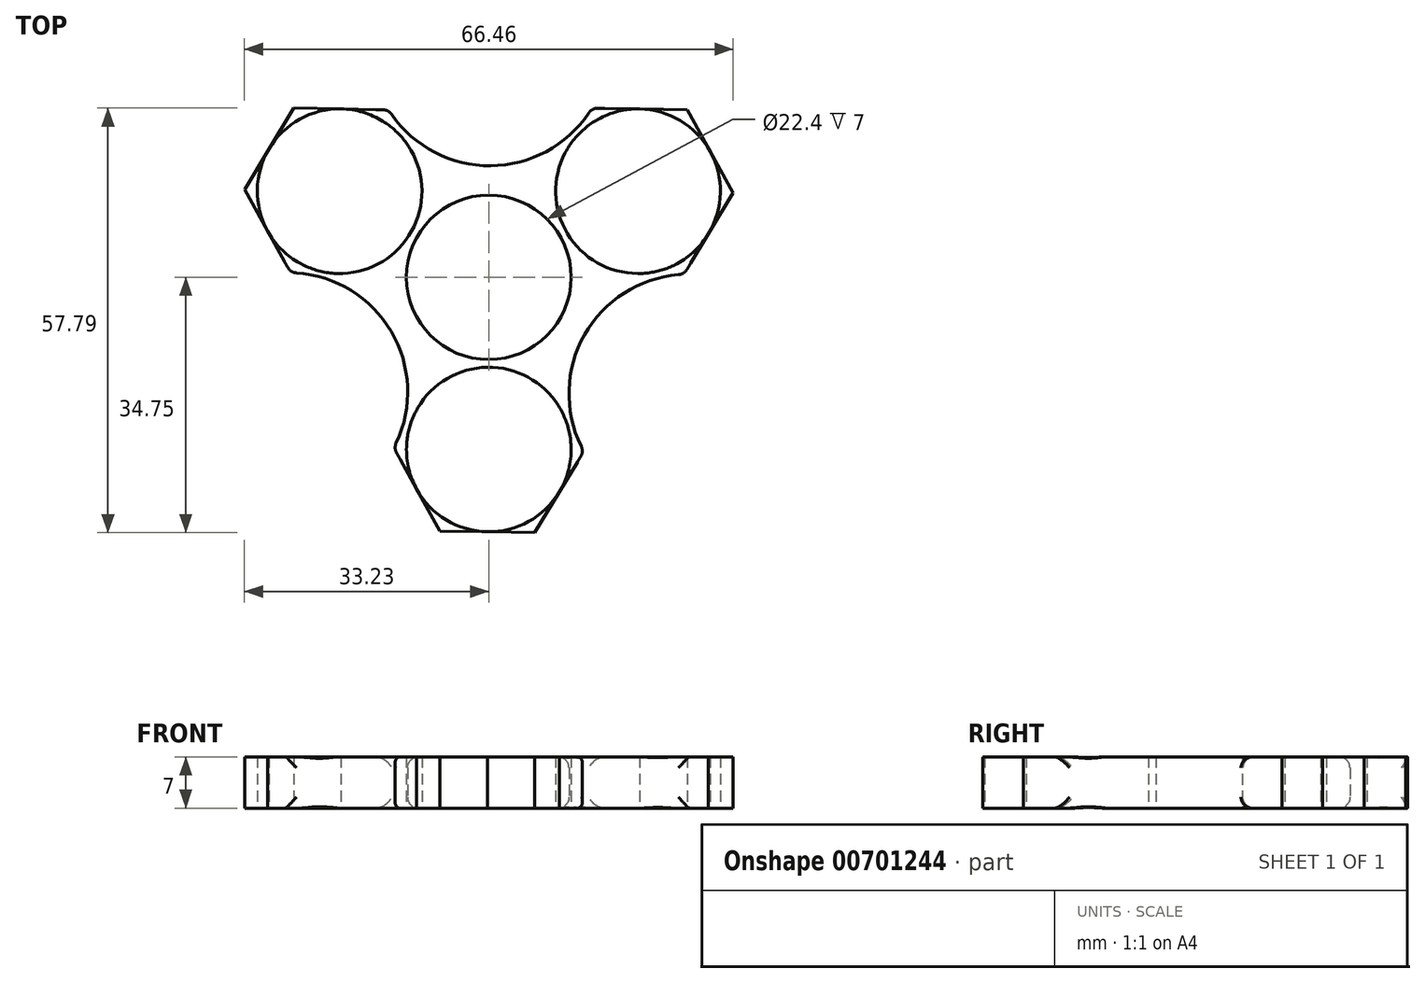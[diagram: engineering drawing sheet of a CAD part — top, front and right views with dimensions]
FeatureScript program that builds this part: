
annotation { "Feature Type Name" : "Feature", "Feature Type Description" : "" }
export const myFeature = defineFeature(function(context is Context, id is Id, definition is map)
    precondition{}
    {
        {
            var Q0;
            Q0=qCreatedBy(makeId("Top.planeOp"),FACE);
            var sketch = newSketch(context, id + "F0", { "sketchPlane" : qUnion([Q0])});
            skCircle(sketch, "E0", {"center": v(0, 0) * mm, "radius": 11.2 * mm});
            skCircle(sketch, "E1.cCircle", {"center": v(0, 0) * mm, "radius": 11.2 * mm, "construction": true});
            skLineSegment(sketch, "E1.0", {"start": v(12.93, -0.08) * mm, "end": v(6.4, -11.24) * mm});
            skLineSegment(sketch, "E1.1", {"start": v(6.4, -11.24) * mm, "end": v(-6.54, -11.16) * mm});
            skLineSegment(sketch, "E1.2", {"start": v(-6.54, -11.16) * mm, "end": v(-12.93, 0.08) * mm});
            skLineSegment(sketch, "E1.3", {"start": v(-12.93, 0.08) * mm, "end": v(-6.4, 11.24) * mm});
            skLineSegment(sketch, "E1.4", {"start": v(-6.4, 11.24) * mm, "end": v(6.54, 11.16) * mm});
            skLineSegment(sketch, "E1.5", {"start": v(6.54, 11.16) * mm, "end": v(12.93, -0.08) * mm});
            skPoint(sketch, "E1.0.midPoint", {"position": v(9.66, -5.66) * mm});
            skCircle(sketch, "E2.cCircle", {"center": v(0, -23.43) * mm, "radius": 11.2 * mm, "construction": true});
            skLineSegment(sketch, "E2.0", {"start": v(-12.93, -23.2) * mm, "end": v(-6.26, -12.12) * mm});
            skLineSegment(sketch, "E2.1", {"start": v(-6.26, -12.12) * mm, "end": v(6.67, -12.36) * mm});
            skLineSegment(sketch, "E2.2", {"start": v(6.67, -12.36) * mm, "end": v(12.93, -23.68) * mm});
            skLineSegment(sketch, "E2.3", {"start": v(12.93, -23.68) * mm, "end": v(6.26, -34.75) * mm});
            skLineSegment(sketch, "E2.4", {"start": v(6.26, -34.75) * mm, "end": v(-6.67, -34.51) * mm});
            skLineSegment(sketch, "E2.5", {"start": v(-6.67, -34.51) * mm, "end": v(-12.93, -23.2) * mm});
            skPoint(sketch, "E2.0.midPoint", {"position": v(-9.6, -17.66) * mm});
            skCircle(sketch, "E3", {"center": v(0, -23.43) * mm, "radius": 11.2 * mm});
            skLineSegment(sketch, "E4.1.0", {"start": v(14.04, 23.04) * mm, "end": v(26.97, 22.8) * mm});
            skLineSegment(sketch, "E4.1.1", {"start": v(26.97, 22.8) * mm, "end": v(33.23, 11.48) * mm});
            skLineSegment(sketch, "E4.1.2", {"start": v(33.23, 11.48) * mm, "end": v(26.55, 0.4) * mm});
            skLineSegment(sketch, "E4.1.3", {"start": v(26.55, 0.4) * mm, "end": v(13.62, 0.64) * mm});
            skLineSegment(sketch, "E4.1.4", {"start": v(13.62, 0.64) * mm, "end": v(7.36, 11.96) * mm});
            skLineSegment(sketch, "E4.1.5", {"start": v(7.36, 11.96) * mm, "end": v(14.04, 23.04) * mm});
            skLineSegment(sketch, "E4.2.0", {"start": v(-26.97, 0.64) * mm, "end": v(-33.23, 11.96) * mm});
            skLineSegment(sketch, "E4.2.1", {"start": v(-33.23, 11.96) * mm, "end": v(-26.55, 23.04) * mm});
            skLineSegment(sketch, "E4.2.2", {"start": v(-26.55, 23.04) * mm, "end": v(-13.62, 22.8) * mm});
            skLineSegment(sketch, "E4.2.3", {"start": v(-13.62, 22.8) * mm, "end": v(-7.36, 11.48) * mm});
            skLineSegment(sketch, "E4.2.4", {"start": v(-7.36, 11.48) * mm, "end": v(-14.04, 0.4) * mm});
            skLineSegment(sketch, "E4.2.5", {"start": v(-14.04, 0.4) * mm, "end": v(-26.97, 0.64) * mm});
            skCircle(sketch, "E5.1.0", {"center": v(20.3, 11.72) * mm, "radius": 11.2 * mm, "construction": true});
            skCircle(sketch, "E5.2.0", {"center": v(-20.3, 11.72) * mm, "radius": 11.2 * mm, "construction": true});
            skLineSegment(sketch, "E6", {"start": v(6.54, 11.16) * mm, "end": v(7.8, 11.16) * mm});
            skLineSegment(sketch, "E7", {"start": v(7.8, 11.16) * mm, "end": v(7.8, 8.93) * mm});
            skLineSegment(sketch, "E8", {"start": v(7.8, 8.93) * mm, "end": v(9.04, 8.93) * mm});
            skLineSegment(sketch, "E9", {"start": v(9.04, 8.93) * mm, "end": v(9.5, 5.97) * mm});
            skLineSegment(sketch, "E10", {"start": v(9.5, 5.97) * mm, "end": v(10.68, 5.97) * mm});
            skLineSegment(sketch, "E11", {"start": v(10.68, 5.97) * mm, "end": v(10.68, 3.88) * mm});
            skLineSegment(sketch, "E12", {"start": v(10.68, 3.88) * mm, "end": v(12.24, 3.14) * mm});
            skLineSegment(sketch, "E13", {"start": v(12.24, 3.14) * mm, "end": v(12.24, 1.14) * mm});
            skLineSegment(sketch, "E14", {"start": v(12.24, 1.14) * mm, "end": v(13.62, 0.64) * mm});
            skLineSegment(sketch, "E15", {"start": v(12.93, -0.08) * mm, "end": v(13.62, 0.64) * mm});
            skLineSegment(sketch, "E16", {"start": v(6.54, 11.16) * mm, "end": v(7.36, 11.96) * mm});
            skLineSegment(sketch, "E17.1.0", {"start": v(-7.1, 10.03) * mm, "end": v(-7.36, 11.48) * mm});
            skLineSegment(sketch, "E17.1.1", {"start": v(-8.84, 9.03) * mm, "end": v(-7.1, 10.03) * mm});
            skLineSegment(sketch, "E17.1.2", {"start": v(-8.7, 7.3) * mm, "end": v(-8.84, 9.03) * mm});
            skLineSegment(sketch, "E17.1.3", {"start": v(-10.5, 6.26) * mm, "end": v(-8.7, 7.3) * mm});
            skLineSegment(sketch, "E17.1.4", {"start": v(-6.4, 11.24) * mm, "end": v(-7.36, 11.48) * mm});
            skLineSegment(sketch, "E17.1.5", {"start": v(-9.91, 5.24) * mm, "end": v(-10.5, 6.26) * mm});
            skLineSegment(sketch, "E17.1.6", {"start": v(-12.25, 3.36) * mm, "end": v(-9.91, 5.24) * mm});
            skLineSegment(sketch, "E17.1.7", {"start": v(-11.64, 2.3) * mm, "end": v(-12.25, 3.36) * mm});
            skLineSegment(sketch, "E17.1.8", {"start": v(-13.57, 1.18) * mm, "end": v(-11.64, 2.3) * mm});
            skLineSegment(sketch, "E17.1.9", {"start": v(-12.93, 0.08) * mm, "end": v(-13.57, 1.18) * mm});
            skLineSegment(sketch, "E17.1.10", {"start": v(-12.93, 0.08) * mm, "end": v(-14.04, 0.4) * mm});
            skLineSegment(sketch, "E17.2.0", {"start": v(-5.14, -11.17) * mm, "end": v(-6.26, -12.12) * mm});
            skLineSegment(sketch, "E17.2.1", {"start": v(-3.4, -12.17) * mm, "end": v(-5.14, -11.17) * mm});
            skLineSegment(sketch, "E17.2.2", {"start": v(-1.98, -11.19) * mm, "end": v(-3.4, -12.17) * mm});
            skLineSegment(sketch, "E17.2.3", {"start": v(-0.17, -12.23) * mm, "end": v(-1.98, -11.19) * mm});
            skLineSegment(sketch, "E17.2.4", {"start": v(-6.54, -11.16) * mm, "end": v(-6.26, -12.12) * mm});
            skLineSegment(sketch, "E17.2.5", {"start": v(0.42, -11.2) * mm, "end": v(-0.17, -12.23) * mm});
            skLineSegment(sketch, "E17.2.6", {"start": v(3.21, -12.3) * mm, "end": v(0.42, -11.2) * mm});
            skLineSegment(sketch, "E17.2.7", {"start": v(3.83, -11.23) * mm, "end": v(3.21, -12.3) * mm});
            skLineSegment(sketch, "E17.2.8", {"start": v(5.76, -12.34) * mm, "end": v(3.83, -11.23) * mm});
            skLineSegment(sketch, "E17.2.9", {"start": v(6.4, -11.24) * mm, "end": v(5.76, -12.34) * mm});
            skLineSegment(sketch, "E17.2.10", {"start": v(6.4, -11.24) * mm, "end": v(6.67, -12.36) * mm});
            skArc(sketch, "E18", {"start": v(-12.93, -23.2) * mm, "mid": v(-13.28, -7.35) * mm, "end": v(-26.97, 0.64) * mm});
            skArc(sketch, "E19.1.0", {"start": v(26.55, 0.4) * mm, "mid": v(13, -7.83) * mm, "end": v(12.93, -23.68) * mm});
            skArc(sketch, "E19.2.0", {"start": v(-13.62, 22.8) * mm, "mid": v(0.28, 15.18) * mm, "end": v(14.04, 23.04) * mm});
            skCircle(sketch, "E20", {"center": v(-20.3, 11.72) * mm, "radius": 11.2 * mm});
            skCircle(sketch, "E21", {"center": v(20.3, 11.72) * mm, "radius": 11.2 * mm});
            skSolve(sketch);
        }
        {
            var Q0;
            {var subQ0=sQuery(id+"F0.wireOp",EDGE,"E2.5");var subQ1=sQuery(id+"F0.wireOp",EDGE,"E2.4");var subQ2=makeQuery(id+"F0.imprint","INTERSECT",VERTEX,{"derivedFrom":[subQ1,subQ0]});Q0=makeQuery(id+"F0.imprint","IMPRINT",FACE,{"disambiguationData":[TD([[makeQuery(id+"F0.imprint","IMPRINT",EDGE,{"disambiguationData":[TD([[subQ2,1.0]])],"derivedFrom":subQ1}),-1.0]])]});}
            var Q1;
            {var subQ0=sQuery(id+"F0.wireOp",EDGE,"E2.4");var subQ1=sQuery(id+"F0.wireOp",EDGE,"E2.3");var subQ2=makeQuery(id+"F0.imprint","INTERSECT",VERTEX,{"derivedFrom":[subQ1,subQ0]});Q1=makeQuery(id+"F0.imprint","IMPRINT",FACE,{"disambiguationData":[TD([[makeQuery(id+"F0.imprint","IMPRINT",EDGE,{"disambiguationData":[TD([[subQ2,1.0]])],"derivedFrom":subQ1}),-1.0]])]});}
            var Q2;
            {var subQ0=sQuery(id+"F0.wireOp",EDGE,"E2.3");var subQ3=sQuery(id+"F0.wireOp",EDGE,"E3");var subQ5=makeQuery(id+"F0.imprint","INTERSECT",VERTEX,{"derivedFrom":[subQ0,subQ3]});Q2=makeQuery(id+"F0.imprint","IMPRINT",FACE,{"disambiguationData":[TD([[makeQuery(id+"F0.imprint","IMPRINT",EDGE,{"disambiguationData":[TD([[subQ5,-1.0]])],"derivedFrom":subQ3}),-1.0]])]});}
            var Q3;
            {var subQ1=sQuery(id+"F0.wireOp",EDGE,"E2.1");var subQ3=sQuery(id+"F0.wireOp",EDGE,"E3");var subQ7=makeQuery(id+"F0.imprint","INTERSECT",VERTEX,{"derivedFrom":[subQ1,subQ3]});Q3=makeQuery(id+"F0.imprint","IMPRINT",FACE,{"disambiguationData":[TD([[makeQuery(id+"F0.imprint","IMPRINT",EDGE,{"disambiguationData":[TD([[subQ7,1.0]])],"derivedFrom":subQ3}),-1.0]])]});}
            var Q4;
            {var subQ0=sQuery(id+"F0.wireOp",EDGE,"E2.5");var subQ3=sQuery(id+"F0.wireOp",EDGE,"E3");var subQ5=makeQuery(id+"F0.imprint","INTERSECT",VERTEX,{"derivedFrom":[subQ0,subQ3]});Q4=makeQuery(id+"F0.imprint","IMPRINT",FACE,{"disambiguationData":[TD([[makeQuery(id+"F0.imprint","IMPRINT",EDGE,{"disambiguationData":[TD([[subQ5,1.0]])],"derivedFrom":subQ3}),-1.0]])]});}
            var Q5;
            {var subQ2=sQuery(id+"F0.wireOp",EDGE,"E3");var subQ5=sQuery(id+"F0.wireOp",EDGE,"E2.0");var subQ7=makeQuery(id+"F0.imprint","INTERSECT",VERTEX,{"derivedFrom":[subQ5,subQ2]});Q5=makeQuery(id+"F0.imprint","IMPRINT",FACE,{"disambiguationData":[TD([[makeQuery(id+"F0.imprint","IMPRINT",EDGE,{"disambiguationData":[TD([[subQ7,1.0]])],"derivedFrom":subQ2}),-1.0]])]});}
            var Q6;
            {var subQ3=sQuery(id+"F0.wireOp",EDGE,"E15");Q6=makeQuery(id+"F0.imprint","IMPRINT",FACE,{"disambiguationData":[TD([[makeQuery(id+"F0.imprint","IMPRINT",EDGE,{"derivedFrom":subQ3}),-1.0]])]});}
            var Q7;
            {var subQ4=sQuery(id+"F0.wireOp",EDGE,"E17.1.10");Q7=makeQuery(id+"F0.imprint","IMPRINT",FACE,{"disambiguationData":[TD([[makeQuery(id+"F0.imprint","IMPRINT",EDGE,{"derivedFrom":subQ4}),1.0]])]});}
            var Q8;
            {var subQ3=sQuery(id+"F0.wireOp",EDGE,"E0");var subQ5=sQuery(id+"F0.wireOp",EDGE,"E1.2");var subQ7=makeQuery(id+"F0.imprint","INTERSECT",VERTEX,{"derivedFrom":[subQ3,subQ5]});Q8=makeQuery(id+"F0.imprint","IMPRINT",FACE,{"disambiguationData":[TD([[makeQuery(id+"F0.imprint","IMPRINT",EDGE,{"disambiguationData":[TD([[subQ7,-1.0]])],"derivedFrom":subQ3}),-1.0]])]});}
            var Q9;
            {var subQ0=sQuery(id+"F0.wireOp",EDGE,"E1.1");var subQ4=sQuery(id+"F0.wireOp",EDGE,"E0");var subQ7=makeQuery(id+"F0.imprint","INTERSECT",VERTEX,{"derivedFrom":[subQ4,subQ0]});Q9=makeQuery(id+"F0.imprint","IMPRINT",FACE,{"disambiguationData":[TD([[makeQuery(id+"F0.imprint","IMPRINT",EDGE,{"disambiguationData":[TD([[subQ7,-1.0]])],"derivedFrom":subQ4}),-1.0]])]});}
            var Q10;
            {var subQ0=sQuery(id+"F0.wireOp",EDGE,"E1.5");var subQ5=sQuery(id+"F0.wireOp",EDGE,"E0");var subQ7=makeQuery(id+"F0.imprint","INTERSECT",VERTEX,{"derivedFrom":[subQ5,subQ0]});Q10=makeQuery(id+"F0.imprint","IMPRINT",FACE,{"disambiguationData":[TD([[makeQuery(id+"F0.imprint","IMPRINT",EDGE,{"disambiguationData":[TD([[subQ7,1.0]])],"derivedFrom":subQ5}),-1.0]])]});}
            var Q11;
            {var subQ1=sQuery(id+"F0.wireOp",EDGE,"E1.4");var subQ4=sQuery(id+"F0.wireOp",EDGE,"E0");var subQ5=makeQuery(id+"F0.imprint","INTERSECT",VERTEX,{"derivedFrom":[subQ4,subQ1]});Q11=makeQuery(id+"F0.imprint","IMPRINT",FACE,{"disambiguationData":[TD([[makeQuery(id+"F0.imprint","IMPRINT",EDGE,{"disambiguationData":[TD([[subQ5,1.0]])],"derivedFrom":subQ4}),-1.0]])]});}
            var Q12;
            {var subQ3=sQuery(id+"F0.wireOp",EDGE,"E0");var subQ5=sQuery(id+"F0.wireOp",EDGE,"E1.4");var subQ7=makeQuery(id+"F0.imprint","INTERSECT",VERTEX,{"derivedFrom":[subQ3,subQ5]});Q12=makeQuery(id+"F0.imprint","IMPRINT",FACE,{"disambiguationData":[TD([[makeQuery(id+"F0.imprint","IMPRINT",EDGE,{"disambiguationData":[TD([[subQ7,-1.0]])],"derivedFrom":subQ3}),-1.0]])]});}
            var Q13;
            {var subQ0=sQuery(id+"F0.wireOp",EDGE,"E1.3");var subQ4=sQuery(id+"F0.wireOp",EDGE,"E0");var subQ7=makeQuery(id+"F0.imprint","INTERSECT",VERTEX,{"derivedFrom":[subQ4,subQ0]});Q13=makeQuery(id+"F0.imprint","IMPRINT",FACE,{"disambiguationData":[TD([[makeQuery(id+"F0.imprint","IMPRINT",EDGE,{"disambiguationData":[TD([[subQ7,-1.0]])],"derivedFrom":subQ4}),-1.0]])]});}
            var Q14;
            {var subQ1=sQuery(id+"F0.wireOp",EDGE,"E4.2.0");var subQ3=sQuery(id+"F0.wireOp",EDGE,"E20");var subQ4=makeQuery(id+"F0.imprint","INTERSECT",VERTEX,{"derivedFrom":[subQ1,subQ3]});Q14=makeQuery(id+"F0.imprint","IMPRINT",FACE,{"disambiguationData":[TD([[makeQuery(id+"F0.imprint","IMPRINT",EDGE,{"disambiguationData":[TD([[subQ4,-1.0]])],"derivedFrom":subQ3}),-1.0]])]});}
            var Q15;
            {var subQ1=sQuery(id+"F0.wireOp",EDGE,"E4.2.4");var subQ3=sQuery(id+"F0.wireOp",EDGE,"E20");var subQ7=makeQuery(id+"F0.imprint","INTERSECT",VERTEX,{"derivedFrom":[subQ1,subQ3]});Q15=makeQuery(id+"F0.imprint","IMPRINT",FACE,{"disambiguationData":[TD([[makeQuery(id+"F0.imprint","IMPRINT",EDGE,{"disambiguationData":[TD([[subQ7,1.0]])],"derivedFrom":subQ3}),-1.0]])]});}
            var Q16;
            {var subQ2=sQuery(id+"F0.wireOp",EDGE,"E20");var subQ5=sQuery(id+"F0.wireOp",EDGE,"E4.2.3");var subQ7=makeQuery(id+"F0.imprint","INTERSECT",VERTEX,{"derivedFrom":[subQ5,subQ2]});Q16=makeQuery(id+"F0.imprint","IMPRINT",FACE,{"disambiguationData":[TD([[makeQuery(id+"F0.imprint","IMPRINT",EDGE,{"disambiguationData":[TD([[subQ7,1.0]])],"derivedFrom":subQ2}),-1.0]])]});}
            var Q17;
            {var subQ1=sQuery(id+"F0.wireOp",EDGE,"E4.2.2");var subQ3=sQuery(id+"F0.wireOp",EDGE,"E20");var subQ4=makeQuery(id+"F0.imprint","INTERSECT",VERTEX,{"derivedFrom":[subQ1,subQ3]});Q17=makeQuery(id+"F0.imprint","IMPRINT",FACE,{"disambiguationData":[TD([[makeQuery(id+"F0.imprint","IMPRINT",EDGE,{"disambiguationData":[TD([[subQ4,1.0]])],"derivedFrom":subQ3}),-1.0]])]});}
            var Q18;
            {var subQ0=sQuery(id+"F0.wireOp",EDGE,"E4.2.2");var subQ1=sQuery(id+"F0.wireOp",EDGE,"E4.2.1");var subQ2=makeQuery(id+"F0.imprint","INTERSECT",VERTEX,{"derivedFrom":[subQ1,subQ0]});Q18=makeQuery(id+"F0.imprint","IMPRINT",FACE,{"disambiguationData":[TD([[makeQuery(id+"F0.imprint","IMPRINT",EDGE,{"disambiguationData":[TD([[subQ2,1.0]])],"derivedFrom":subQ1}),-1.0]])]});}
            var Q19;
            {var subQ0=sQuery(id+"F0.wireOp",EDGE,"E4.2.1");var subQ1=sQuery(id+"F0.wireOp",EDGE,"E4.2.0");var subQ2=makeQuery(id+"F0.imprint","INTERSECT",VERTEX,{"derivedFrom":[subQ1,subQ0]});Q19=makeQuery(id+"F0.imprint","IMPRINT",FACE,{"disambiguationData":[TD([[makeQuery(id+"F0.imprint","IMPRINT",EDGE,{"disambiguationData":[TD([[subQ2,1.0]])],"derivedFrom":subQ1}),-1.0]])]});}
            var Q20;
            {var subQ0=sQuery(id+"F0.wireOp",EDGE,"E16");Q20=makeQuery(id+"F0.imprint","IMPRINT",FACE,{"disambiguationData":[TD([[makeQuery(id+"F0.imprint","IMPRINT",EDGE,{"derivedFrom":subQ0}),1.0]])]});}
            var Q21;
            {var subQ1=sQuery(id+"F0.wireOp",EDGE,"E4.1.4");var subQ3=sQuery(id+"F0.wireOp",EDGE,"E21");var subQ7=makeQuery(id+"F0.imprint","INTERSECT",VERTEX,{"derivedFrom":[subQ1,subQ3]});Q21=makeQuery(id+"F0.imprint","IMPRINT",FACE,{"disambiguationData":[TD([[makeQuery(id+"F0.imprint","IMPRINT",EDGE,{"disambiguationData":[TD([[subQ7,1.0]])],"derivedFrom":subQ3}),-1.0]])]});}
            var Q22;
            {var subQ2=sQuery(id+"F0.wireOp",EDGE,"E21");var subQ5=sQuery(id+"F0.wireOp",EDGE,"E4.1.3");var subQ7=makeQuery(id+"F0.imprint","INTERSECT",VERTEX,{"derivedFrom":[subQ5,subQ2]});Q22=makeQuery(id+"F0.imprint","IMPRINT",FACE,{"disambiguationData":[TD([[makeQuery(id+"F0.imprint","IMPRINT",EDGE,{"disambiguationData":[TD([[subQ7,1.0]])],"derivedFrom":subQ2}),-1.0]])]});}
            var Q23;
            {var subQ1=sQuery(id+"F0.wireOp",EDGE,"E4.1.2");var subQ3=sQuery(id+"F0.wireOp",EDGE,"E21");var subQ4=makeQuery(id+"F0.imprint","INTERSECT",VERTEX,{"derivedFrom":[subQ1,subQ3]});Q23=makeQuery(id+"F0.imprint","IMPRINT",FACE,{"disambiguationData":[TD([[makeQuery(id+"F0.imprint","IMPRINT",EDGE,{"disambiguationData":[TD([[subQ4,1.0]])],"derivedFrom":subQ3}),-1.0]])]});}
            var Q24;
            {var subQ0=sQuery(id+"F0.wireOp",EDGE,"E4.1.2");var subQ1=sQuery(id+"F0.wireOp",EDGE,"E4.1.1");var subQ2=makeQuery(id+"F0.imprint","INTERSECT",VERTEX,{"derivedFrom":[subQ1,subQ0]});Q24=makeQuery(id+"F0.imprint","IMPRINT",FACE,{"disambiguationData":[TD([[makeQuery(id+"F0.imprint","IMPRINT",EDGE,{"disambiguationData":[TD([[subQ2,1.0]])],"derivedFrom":subQ1}),-1.0]])]});}
            var Q25;
            {var subQ0=sQuery(id+"F0.wireOp",EDGE,"E4.1.1");var subQ1=sQuery(id+"F0.wireOp",EDGE,"E4.1.0");var subQ2=makeQuery(id+"F0.imprint","INTERSECT",VERTEX,{"derivedFrom":[subQ1,subQ0]});Q25=makeQuery(id+"F0.imprint","IMPRINT",FACE,{"disambiguationData":[TD([[makeQuery(id+"F0.imprint","IMPRINT",EDGE,{"disambiguationData":[TD([[subQ2,1.0]])],"derivedFrom":subQ1}),-1.0]])]});}
            var Q26;
            {var subQ1=sQuery(id+"F0.wireOp",EDGE,"E4.1.0");var subQ3=sQuery(id+"F0.wireOp",EDGE,"E21");var subQ4=makeQuery(id+"F0.imprint","INTERSECT",VERTEX,{"derivedFrom":[subQ1,subQ3]});Q26=makeQuery(id+"F0.imprint","IMPRINT",FACE,{"disambiguationData":[TD([[makeQuery(id+"F0.imprint","IMPRINT",EDGE,{"disambiguationData":[TD([[subQ4,-1.0]])],"derivedFrom":subQ3}),-1.0]])]});}
            var Q27;
            {var subQ2=sQuery(id+"F0.wireOp",EDGE,"E14");Q27=makeQuery(id+"F0.imprint","IMPRINT",FACE,{"disambiguationData":[TD([[makeQuery(id+"F0.imprint","IMPRINT",EDGE,{"derivedFrom":subQ2}),-1.0]])]});}
            var Q28;
            {var subQ2=sQuery(id+"F0.wireOp",EDGE,"E13");Q28=makeQuery(id+"F0.imprint","IMPRINT",FACE,{"disambiguationData":[TD([[makeQuery(id+"F0.imprint","IMPRINT",EDGE,{"derivedFrom":subQ2}),1.0]])]});}
            var Q29;
            {var subQ0=sQuery(id+"F0.wireOp",EDGE,"E12");Q29=makeQuery(id+"F0.imprint","IMPRINT",FACE,{"disambiguationData":[TD([[makeQuery(id+"F0.imprint","IMPRINT",EDGE,{"derivedFrom":subQ0}),-1.0]])]});}
            var Q30;
            {var subQ0=sQuery(id+"F0.wireOp",EDGE,"E11");Q30=makeQuery(id+"F0.imprint","IMPRINT",FACE,{"disambiguationData":[TD([[makeQuery(id+"F0.imprint","IMPRINT",EDGE,{"derivedFrom":subQ0}),1.0]])]});}
            var Q31;
            {var subQ0=sQuery(id+"F0.wireOp",EDGE,"E10");Q31=makeQuery(id+"F0.imprint","IMPRINT",FACE,{"disambiguationData":[TD([[makeQuery(id+"F0.imprint","IMPRINT",EDGE,{"derivedFrom":subQ0}),-1.0]])]});}
            var Q32;
            {var subQ3=sQuery(id+"F0.wireOp",EDGE,"E9");Q32=makeQuery(id+"F0.imprint","IMPRINT",FACE,{"disambiguationData":[TD([[makeQuery(id+"F0.imprint","IMPRINT",EDGE,{"derivedFrom":subQ3}),1.0]])]});}
            var Q33;
            {var subQ0=sQuery(id+"F0.wireOp",EDGE,"E8");Q33=makeQuery(id+"F0.imprint","IMPRINT",FACE,{"disambiguationData":[TD([[makeQuery(id+"F0.imprint","IMPRINT",EDGE,{"derivedFrom":subQ0}),-1.0]])]});}
            var Q34;
            {var subQ0=sQuery(id+"F0.wireOp",EDGE,"E7");Q34=makeQuery(id+"F0.imprint","IMPRINT",FACE,{"disambiguationData":[TD([[makeQuery(id+"F0.imprint","IMPRINT",EDGE,{"derivedFrom":subQ0}),1.0]])]});}
            var Q35;
            {var subQ0=sQuery(id+"F0.wireOp",EDGE,"E6");Q35=makeQuery(id+"F0.imprint","IMPRINT",FACE,{"disambiguationData":[TD([[makeQuery(id+"F0.imprint","IMPRINT",EDGE,{"derivedFrom":subQ0}),-1.0]])]});}
            var Q36;
            {var subQ0=sQuery(id+"F0.wireOp",EDGE,"E17.2.5");Q36=makeQuery(id+"F0.imprint","IMPRINT",FACE,{"disambiguationData":[TD([[makeQuery(id+"F0.imprint","IMPRINT",EDGE,{"derivedFrom":subQ0}),1.0]])]});}
            var Q37;
            {var subQ0=sQuery(id+"F0.wireOp",EDGE,"E17.2.6");Q37=makeQuery(id+"F0.imprint","IMPRINT",FACE,{"disambiguationData":[TD([[makeQuery(id+"F0.imprint","IMPRINT",EDGE,{"derivedFrom":subQ0}),-1.0]])]});}
            var Q38;
            {var subQ0=sQuery(id+"F0.wireOp",EDGE,"E17.2.7");Q38=makeQuery(id+"F0.imprint","IMPRINT",FACE,{"disambiguationData":[TD([[makeQuery(id+"F0.imprint","IMPRINT",EDGE,{"derivedFrom":subQ0}),1.0]])]});}
            var Q39;
            {var subQ2=sQuery(id+"F0.wireOp",EDGE,"E17.2.8");Q39=makeQuery(id+"F0.imprint","IMPRINT",FACE,{"disambiguationData":[TD([[makeQuery(id+"F0.imprint","IMPRINT",EDGE,{"derivedFrom":subQ2}),-1.0]])]});}
            var Q40;
            {var subQ2=sQuery(id+"F0.wireOp",EDGE,"E17.2.0");Q40=makeQuery(id+"F0.imprint","IMPRINT",FACE,{"disambiguationData":[TD([[makeQuery(id+"F0.imprint","IMPRINT",EDGE,{"derivedFrom":subQ2}),-1.0]])]});}
            var Q41;
            {var subQ0=sQuery(id+"F0.wireOp",EDGE,"E17.2.0");Q41=makeQuery(id+"F0.imprint","IMPRINT",FACE,{"disambiguationData":[TD([[makeQuery(id+"F0.imprint","IMPRINT",EDGE,{"derivedFrom":subQ0}),1.0]])]});}
            var Q42;
            {var subQ0=sQuery(id+"F0.wireOp",EDGE,"E17.2.1");Q42=makeQuery(id+"F0.imprint","IMPRINT",FACE,{"disambiguationData":[TD([[makeQuery(id+"F0.imprint","IMPRINT",EDGE,{"derivedFrom":subQ0}),-1.0]])]});}
            var Q43;
            {var subQ0=sQuery(id+"F0.wireOp",EDGE,"E17.2.2");Q43=makeQuery(id+"F0.imprint","IMPRINT",FACE,{"disambiguationData":[TD([[makeQuery(id+"F0.imprint","IMPRINT",EDGE,{"derivedFrom":subQ0}),1.0]])]});}
            var Q44;
            {var subQ3=sQuery(id+"F0.wireOp",EDGE,"E17.2.3");Q44=makeQuery(id+"F0.imprint","IMPRINT",FACE,{"disambiguationData":[TD([[makeQuery(id+"F0.imprint","IMPRINT",EDGE,{"derivedFrom":subQ3}),-1.0]])]});}
            var Q45;
            {var subQ2=sQuery(id+"F0.wireOp",EDGE,"E17.2.9");Q45=makeQuery(id+"F0.imprint","IMPRINT",FACE,{"disambiguationData":[TD([[makeQuery(id+"F0.imprint","IMPRINT",EDGE,{"derivedFrom":subQ2}),1.0]])]});}
            var Q46;
            {var subQ2=sQuery(id+"F0.wireOp",EDGE,"E17.1.9");Q46=makeQuery(id+"F0.imprint","IMPRINT",FACE,{"disambiguationData":[TD([[makeQuery(id+"F0.imprint","IMPRINT",EDGE,{"derivedFrom":subQ2}),1.0]])]});}
            var Q47;
            {var subQ2=sQuery(id+"F0.wireOp",EDGE,"E17.1.8");Q47=makeQuery(id+"F0.imprint","IMPRINT",FACE,{"disambiguationData":[TD([[makeQuery(id+"F0.imprint","IMPRINT",EDGE,{"derivedFrom":subQ2}),-1.0]])]});}
            var Q48;
            {var subQ0=sQuery(id+"F0.wireOp",EDGE,"E17.1.7");Q48=makeQuery(id+"F0.imprint","IMPRINT",FACE,{"disambiguationData":[TD([[makeQuery(id+"F0.imprint","IMPRINT",EDGE,{"derivedFrom":subQ0}),1.0]])]});}
            var Q49;
            {var subQ0=sQuery(id+"F0.wireOp",EDGE,"E17.1.6");Q49=makeQuery(id+"F0.imprint","IMPRINT",FACE,{"disambiguationData":[TD([[makeQuery(id+"F0.imprint","IMPRINT",EDGE,{"derivedFrom":subQ0}),-1.0]])]});}
            var Q50;
            {var subQ0=sQuery(id+"F0.wireOp",EDGE,"E17.1.5");Q50=makeQuery(id+"F0.imprint","IMPRINT",FACE,{"disambiguationData":[TD([[makeQuery(id+"F0.imprint","IMPRINT",EDGE,{"derivedFrom":subQ0}),1.0]])]});}
            var Q51;
            {var subQ3=sQuery(id+"F0.wireOp",EDGE,"E17.1.3");Q51=makeQuery(id+"F0.imprint","IMPRINT",FACE,{"disambiguationData":[TD([[makeQuery(id+"F0.imprint","IMPRINT",EDGE,{"derivedFrom":subQ3}),-1.0]])]});}
            var Q52;
            {var subQ2=sQuery(id+"F0.wireOp",EDGE,"E6");Q52=makeQuery(id+"F0.imprint","IMPRINT",FACE,{"disambiguationData":[TD([[makeQuery(id+"F0.imprint","IMPRINT",EDGE,{"derivedFrom":subQ2}),1.0]])]});}
            var Q53;
            {var subQ2=sQuery(id+"F0.wireOp",EDGE,"E17.1.0");Q53=makeQuery(id+"F0.imprint","IMPRINT",FACE,{"disambiguationData":[TD([[makeQuery(id+"F0.imprint","IMPRINT",EDGE,{"derivedFrom":subQ2}),-1.0]])]});}
            var Q54;
            {var subQ0=sQuery(id+"F0.wireOp",EDGE,"E17.1.0");Q54=makeQuery(id+"F0.imprint","IMPRINT",FACE,{"disambiguationData":[TD([[makeQuery(id+"F0.imprint","IMPRINT",EDGE,{"derivedFrom":subQ0}),1.0]])]});}
            var Q55;
            {var subQ0=sQuery(id+"F0.wireOp",EDGE,"E17.1.2");Q55=makeQuery(id+"F0.imprint","IMPRINT",FACE,{"disambiguationData":[TD([[makeQuery(id+"F0.imprint","IMPRINT",EDGE,{"derivedFrom":subQ0}),1.0]])]});}
            var Q56;
            {var subQ0=sQuery(id+"F0.wireOp",EDGE,"E17.1.1");Q56=makeQuery(id+"F0.imprint","IMPRINT",FACE,{"disambiguationData":[TD([[makeQuery(id+"F0.imprint","IMPRINT",EDGE,{"derivedFrom":subQ0}),-1.0]])]});}
            extrude(context, id + "F1", {"entities" : qUnion([Q0, Q1, Q2, Q3, Q4, Q5, Q6, Q7, Q8, Q9, Q10, Q11, Q12, Q13, Q14, Q15, Q16, Q17, Q18, Q19, Q20, Q21, Q22, Q23, Q24, Q25, Q26, Q27, Q28, Q29, Q30, Q31, Q32, Q33, Q34, Q35, Q36, Q37, Q38, Q39, Q40, Q41, Q42, Q43, Q44, Q45, Q46, Q47, Q48, Q49, Q50, Q51, Q52, Q53, Q54, Q55, Q56]), "depth" : 7 * mm, "offsetDistance" : 25 * mm});
        }
        {
            var Q0;
            Q0=makeQuery(id+"F1.opExtrude","SWEPT_FACE",FACE,{"disambiguationData":[OSD([sQuery(id+"F0.wireOp",EDGE,"E19.1.0")])]});
            var Q1;
            Q1=makeQuery(id+"F1.opExtrude","SWEPT_FACE",FACE,{"disambiguationData":[OSD([sQuery(id+"F0.wireOp",EDGE,"E18")])]});
            var Q2;
            Q2=makeQuery(id+"F1.opExtrude","SWEPT_FACE",FACE,{"disambiguationData":[OSD([sQuery(id+"F0.wireOp",EDGE,"E19.2.0")])]});
            fillet(context, id + "F2", {"entities" : qUnion([Q0, Q1, Q2]), "radius" : 1.5 * mm, "tangentPropagation" : true, "allowEdgeOverflow" : false});
        }
    });
